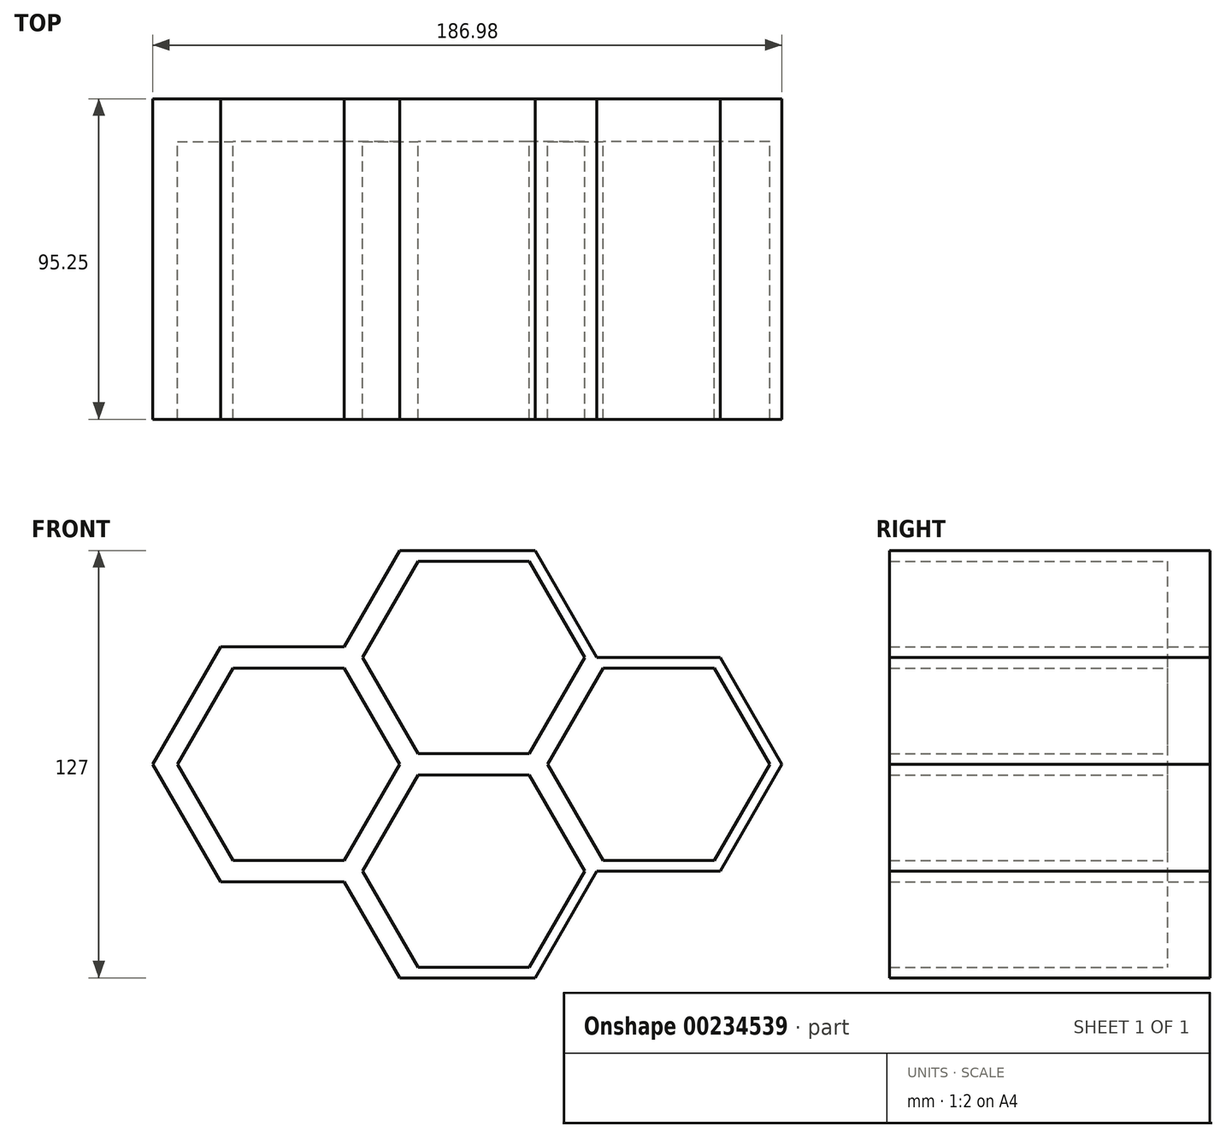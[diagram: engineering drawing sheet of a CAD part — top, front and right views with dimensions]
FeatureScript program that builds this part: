
annotation { "Feature Type Name" : "Feature", "Feature Type Description" : "" }
export const myFeature = defineFeature(function(context is Context, id is Id, definition is map)
    precondition{}
    {
        {
            var Q0;
            Q0=qCreatedBy(makeId("Front.planeOp"),FACE);
            var sketch = newSketch(context, id + "F0", { "sketchPlane" : qUnion([Q0])});
            skLineSegment(sketch, "E0.0", {"start": v(-77.6, 35.04) * mm, "end": v(-59.27, 66.8) * mm});
            skLineSegment(sketch, "E1.0", {"start": v(-132.6, 3.3) * mm, "end": v(-114.26, 35.04) * mm});
            skLineSegment(sketch, "E1.1", {"start": v(-114.26, 35.04) * mm, "end": v(-77.6, 35.04) * mm});
            skPoint(sketch, "E1.0.midPoint", {"position": v(-123.43, 19.17) * mm});
            skCircle(sketch, "E2.cCircle", {"center": v(-150.93, 35.04) * mm, "radius": 28.58 * mm, "construction": true});
            skLineSegment(sketch, "E2.0", {"start": v(-183.92, 35.04) * mm, "end": v(-167.42, 63.62) * mm});
            skLineSegment(sketch, "E2.1", {"start": v(-167.42, 63.62) * mm, "end": v(-134.43, 63.62) * mm});
            skLineSegment(sketch, "E2.2", {"start": v(-134.43, 63.62) * mm, "end": v(-117.93, 35.04) * mm});
            skLineSegment(sketch, "E2.3", {"start": v(-117.93, 35.04) * mm, "end": v(-134.43, 6.47) * mm});
            skLineSegment(sketch, "E2.4", {"start": v(-134.43, 6.47) * mm, "end": v(-167.42, 6.47) * mm});
            skLineSegment(sketch, "E2.5", {"start": v(-167.42, 6.47) * mm, "end": v(-183.92, 35.04) * mm});
            skPoint(sketch, "E2.0.midPoint", {"position": v(-175.67, 49.33) * mm});
            skCircle(sketch, "E3.cCircle", {"center": v(-150.93, 35.04) * mm, "radius": 31.75 * mm, "construction": true});
            skLineSegment(sketch, "E3.0", {"start": v(-187.59, 35.04) * mm, "end": v(-169.26, 66.8) * mm});
            skLineSegment(sketch, "E3.1", {"start": v(-169.26, 66.8) * mm, "end": v(-132.6, 66.8) * mm});
            skLineSegment(sketch, "E3.2", {"start": v(-132.6, 66.8) * mm, "end": v(-114.26, 35.04) * mm});
            skLineSegment(sketch, "E3.3", {"start": v(-114.26, 35.04) * mm, "end": v(-132.6, 3.3) * mm});
            skLineSegment(sketch, "E3.4", {"start": v(-132.6, 3.3) * mm, "end": v(-169.26, 3.3) * mm});
            skLineSegment(sketch, "E3.5", {"start": v(-169.26, 3.3) * mm, "end": v(-187.59, 35.04) * mm});
            skPoint(sketch, "E3.0.midPoint", {"position": v(-178.42, 50.92) * mm});
            skLineSegment(sketch, "E4.1", {"start": v(-221.8, 35.04) * mm, "end": v(-187.59, 35.04) * mm});
            skCircle(sketch, "E5.cCircle", {"center": v(-95.93, 66.8) * mm, "radius": 28.58 * mm, "construction": true});
            skLineSegment(sketch, "E5.0", {"start": v(-128.93, 66.8) * mm, "end": v(-112.43, 95.37) * mm});
            skLineSegment(sketch, "E5.1", {"start": v(-112.43, 95.37) * mm, "end": v(-79.43, 95.37) * mm});
            skLineSegment(sketch, "E5.2", {"start": v(-79.43, 95.37) * mm, "end": v(-62.94, 66.8) * mm});
            skLineSegment(sketch, "E5.3", {"start": v(-62.94, 66.8) * mm, "end": v(-79.43, 38.22) * mm});
            skLineSegment(sketch, "E5.4", {"start": v(-79.43, 38.22) * mm, "end": v(-112.43, 38.22) * mm});
            skLineSegment(sketch, "E5.5", {"start": v(-112.43, 38.22) * mm, "end": v(-128.93, 66.8) * mm});
            skPoint(sketch, "E5.0.midPoint", {"position": v(-120.68, 81.08) * mm});
            skCircle(sketch, "E6.cCircle", {"center": v(-95.93, 66.8) * mm, "radius": 31.75 * mm, "construction": true});
            skLineSegment(sketch, "E6.0", {"start": v(-132.6, 66.8) * mm, "end": v(-114.26, 98.54) * mm});
            skLineSegment(sketch, "E6.1", {"start": v(-114.26, 98.54) * mm, "end": v(-77.6, 98.54) * mm});
            skLineSegment(sketch, "E6.2", {"start": v(-77.6, 98.54) * mm, "end": v(-59.27, 66.8) * mm});
            skLineSegment(sketch, "E6.3", {"start": v(-59.27, 66.8) * mm, "end": v(-77.6, 35.04) * mm});
            skLineSegment(sketch, "E6.4", {"start": v(-77.6, 35.04) * mm, "end": v(-114.26, 35.04) * mm});
            skLineSegment(sketch, "E6.5", {"start": v(-114.26, 35.04) * mm, "end": v(-132.6, 66.8) * mm});
            skPoint(sketch, "E6.0.midPoint", {"position": v(-123.43, 82.67) * mm});
            skCircle(sketch, "E7.cCircle", {"center": v(-205.92, 66.8) * mm, "radius": 28.57 * mm, "construction": true});
            skLineSegment(sketch, "E7.0", {"start": v(-238.91, 66.8) * mm, "end": v(-222.42, 95.37) * mm});
            skLineSegment(sketch, "E7.1", {"start": v(-222.42, 95.37) * mm, "end": v(-189.42, 95.37) * mm});
            skLineSegment(sketch, "E7.2", {"start": v(-189.42, 95.37) * mm, "end": v(-172.92, 66.8) * mm});
            skLineSegment(sketch, "E7.3", {"start": v(-172.92, 66.8) * mm, "end": v(-189.42, 38.22) * mm});
            skLineSegment(sketch, "E7.4", {"start": v(-189.42, 38.22) * mm, "end": v(-222.42, 38.22) * mm});
            skLineSegment(sketch, "E7.5", {"start": v(-222.42, 38.22) * mm, "end": v(-238.91, 66.8) * mm});
            skPoint(sketch, "E7.0.midPoint", {"position": v(-230.66, 81.08) * mm});
            skCircle(sketch, "E8.cCircle", {"center": v(-205.92, 66.8) * mm, "radius": 31.75 * mm, "construction": true});
            skLineSegment(sketch, "E8.0", {"start": v(-242.58, 66.8) * mm, "end": v(-224.25, 98.54) * mm});
            skLineSegment(sketch, "E8.1", {"start": v(-224.25, 98.54) * mm, "end": v(-187.59, 98.54) * mm});
            skLineSegment(sketch, "E8.2", {"start": v(-187.59, 98.54) * mm, "end": v(-169.26, 66.8) * mm});
            skLineSegment(sketch, "E8.3", {"start": v(-169.26, 66.8) * mm, "end": v(-187.59, 35.04) * mm});
            skLineSegment(sketch, "E8.4", {"start": v(-187.59, 35.04) * mm, "end": v(-224.25, 35.04) * mm});
            skLineSegment(sketch, "E8.5", {"start": v(-224.25, 35.04) * mm, "end": v(-242.58, 66.8) * mm});
            skPoint(sketch, "E8.0.midPoint", {"position": v(-233.41, 82.67) * mm});
            skCircle(sketch, "E9.cCircle", {"center": v(-150.93, 98.54) * mm, "radius": 28.58 * mm, "construction": true});
            skLineSegment(sketch, "E9.0", {"start": v(-183.92, 98.54) * mm, "end": v(-167.42, 127.12) * mm});
            skLineSegment(sketch, "E9.1", {"start": v(-167.42, 127.12) * mm, "end": v(-134.43, 127.12) * mm});
            skLineSegment(sketch, "E9.2", {"start": v(-134.43, 127.12) * mm, "end": v(-117.93, 98.54) * mm});
            skLineSegment(sketch, "E9.3", {"start": v(-117.93, 98.54) * mm, "end": v(-134.43, 69.97) * mm});
            skLineSegment(sketch, "E9.4", {"start": v(-134.43, 69.97) * mm, "end": v(-167.42, 69.97) * mm});
            skLineSegment(sketch, "E9.5", {"start": v(-167.42, 69.97) * mm, "end": v(-183.92, 98.54) * mm});
            skPoint(sketch, "E9.0.midPoint", {"position": v(-175.67, 112.83) * mm});
            skCircle(sketch, "E10.cCircle", {"center": v(-150.93, 98.54) * mm, "radius": 31.75 * mm, "construction": true});
            skLineSegment(sketch, "E10.0", {"start": v(-187.59, 98.54) * mm, "end": v(-169.26, 130.3) * mm});
            skLineSegment(sketch, "E10.1", {"start": v(-169.26, 130.3) * mm, "end": v(-132.6, 130.3) * mm});
            skLineSegment(sketch, "E10.2", {"start": v(-132.6, 130.3) * mm, "end": v(-114.26, 98.54) * mm});
            skLineSegment(sketch, "E10.3", {"start": v(-114.26, 98.54) * mm, "end": v(-132.6, 66.8) * mm});
            skLineSegment(sketch, "E10.4", {"start": v(-132.6, 66.8) * mm, "end": v(-169.26, 66.8) * mm});
            skLineSegment(sketch, "E10.5", {"start": v(-169.26, 66.8) * mm, "end": v(-187.59, 98.54) * mm});
            skPoint(sketch, "E10.0.midPoint", {"position": v(-178.42, 114.42) * mm});
            skLineSegment(sketch, "E11.5", {"start": v(-59.27, 66.8) * mm, "end": v(-77.6, 98.54) * mm});
            skLineSegment(sketch, "E12.4", {"start": v(-77.6, 98.54) * mm, "end": v(-114.26, 98.54) * mm});
            skLineSegment(sketch, "E12.5", {"start": v(-114.26, 98.54) * mm, "end": v(-132.6, 130.3) * mm});
            skLineSegment(sketch, "E13.1", {"start": v(-169.26, 3.3) * mm, "end": v(-132.6, 3.3) * mm});
            skLineSegment(sketch, "E14.4", {"start": v(-190.64, 98.54) * mm, "end": v(-224.25, 98.54) * mm});
            skLineSegment(sketch, "E15.4", {"start": v(-132.6, 130.3) * mm, "end": v(-169.26, 130.3) * mm});
            skLineSegment(sketch, "E16", {"start": v(-172.92, 130.3) * mm, "end": v(-189.42, 101.72) * mm});
            skLineSegment(sketch, "E17", {"start": v(-189.42, 101.72) * mm, "end": v(-226.08, 101.72) * mm});
            skLineSegment(sketch, "E18", {"start": v(-226.08, 101.72) * mm, "end": v(-246.25, 66.8) * mm});
            skLineSegment(sketch, "E19", {"start": v(-246.25, 66.8) * mm, "end": v(-226.08, 31.87) * mm});
            skLineSegment(sketch, "E20", {"start": v(-226.08, 31.87) * mm, "end": v(-189.42, 31.87) * mm});
            skLineSegment(sketch, "E21", {"start": v(-189.42, 31.87) * mm, "end": v(-172.92, 3.3) * mm});
            skLineSegment(sketch, "E22", {"start": v(-73.94, 98.54) * mm, "end": v(-57.44, 69.97) * mm});
            skLineSegment(sketch, "E23", {"start": v(-172.92, 3.3) * mm, "end": v(-169.26, 3.3) * mm});
            skLineSegment(sketch, "E24", {"start": v(-169.26, 130.3) * mm, "end": v(-172.92, 130.3) * mm});
            skLineSegment(sketch, "E25", {"start": v(-57.44, 69.97) * mm, "end": v(-59.27, 66.8) * mm});
            skLineSegment(sketch, "E26", {"start": v(-73.94, 98.54) * mm, "end": v(-77.6, 98.54) * mm});
            skSolve(sketch);
        }
        {
            var Q0;
            Q0=makeQuery(id+"F0.imprint","IMPRINT",FACE,{"disambiguationData":[TD([[makeQuery(id+"F0.imprint","IMPRINT",EDGE,{"derivedFrom":sQuery(id+"F0.wireOp",EDGE,"68d16a58-0471-4e1c-b2b3-2a61df7c0d9d.0")}),-1.0]])]});
            var Q1;
            Q1=makeQuery(id+"F0.imprint","IMPRINT",FACE,{"disambiguationData":[TD([[makeQuery(id+"F0.imprint","IMPRINT",EDGE,{"derivedFrom":sQuery(id+"F0.wireOp",EDGE,"ae29455d-c252-400a-b569-c5a1c48e1351.0")}),-1.0]])]});
            var Q2;
            Q2=makeQuery(id+"F0.imprint","IMPRINT",FACE,{"disambiguationData":[TD([[makeQuery(id+"F0.imprint","IMPRINT",EDGE,{"derivedFrom":sQuery(id+"F0.wireOp",EDGE,"cad1e4f3-bd43-45ec-b31a-1d5006939c94.0")}),-1.0]])]});
            var Q3;
            Q3=makeQuery(id+"F0.imprint","IMPRINT",FACE,{"disambiguationData":[TD([[makeQuery(id+"F0.imprint","IMPRINT",EDGE,{"derivedFrom":sQuery(id+"F0.wireOp",EDGE,"b43d4d8c-f78a-4ff8-8565-99a66ce6ec5f.0")}),-1.0]])]});
            var Q4;
            Q4=makeQuery(id+"F0.imprint","IMPRINT",FACE,{"disambiguationData":[TD([[makeQuery(id+"F0.imprint","IMPRINT",EDGE,{"derivedFrom":sQuery(id+"F0.wireOp",EDGE,"8c75d941-d110-4871-aa41-90a72d60fb2b.0")}),-1.0]])]});
            var Q5;
            Q5=makeQuery(id+"F0.imprint","IMPRINT",FACE,{"disambiguationData":[TD([[makeQuery(id+"F0.imprint","IMPRINT",EDGE,{"derivedFrom":sQuery(id+"F0.wireOp",EDGE,"258573fa-3544-418e-8bc5-5d37e5b8ba09.0")}),-1.0]])]});
            var Q6;
            Q6=makeQuery(id+"F0.imprint","IMPRINT",FACE,{"disambiguationData":[TD([[makeQuery(id+"F0.imprint","IMPRINT",EDGE,{"derivedFrom":sQuery(id+"F0.wireOp",EDGE,"E7.0")}),-1.0]])]});
            var Q7;
            Q7=makeQuery(id+"F0.imprint","IMPRINT",FACE,{"disambiguationData":[TD([[makeQuery(id+"F0.imprint","IMPRINT",EDGE,{"derivedFrom":sQuery(id+"F0.wireOp",EDGE,"93717492-86db-456f-ae55-f71e4e93837b.0")}),-1.0]])]});
            var Q8;
            Q8=makeQuery(id+"F0.imprint","IMPRINT",FACE,{"disambiguationData":[TD([[makeQuery(id+"F0.imprint","IMPRINT",EDGE,{"derivedFrom":sQuery(id+"F0.wireOp",EDGE,"E9.0")}),-1.0]])]});
            var Q9;
            Q9=makeQuery(id+"F0.imprint","IMPRINT",FACE,{"disambiguationData":[TD([[makeQuery(id+"F0.imprint","IMPRINT",EDGE,{"derivedFrom":sQuery(id+"F0.wireOp",EDGE,"0306a0a6-7289-4661-a415-5fa5585f2cb5.0")}),-1.0]])]});
            var Q10;
            Q10=makeQuery(id+"F0.imprint","IMPRINT",FACE,{"disambiguationData":[TD([[makeQuery(id+"F0.imprint","IMPRINT",EDGE,{"derivedFrom":sQuery(id+"F0.wireOp",EDGE,"0a91a14e-ea0c-483f-91eb-c48bd73cb0e6.0")}),-1.0]])]});
            var Q11;
            Q11=makeQuery(id+"F0.imprint","IMPRINT",FACE,{"disambiguationData":[TD([[makeQuery(id+"F0.imprint","IMPRINT",EDGE,{"derivedFrom":sQuery(id+"F0.wireOp",EDGE,"cbfd9497-f7fe-4f18-9288-d90aa8075d81.0")}),-1.0]])]});
            var Q12;
            Q12=makeQuery(id+"F0.imprint","IMPRINT",FACE,{"disambiguationData":[TD([[makeQuery(id+"F0.imprint","IMPRINT",EDGE,{"derivedFrom":sQuery(id+"F0.wireOp",EDGE,"6282d196-dd8f-4bb0-bca4-b9108e277473.0")}),-1.0]])]});
            var Q13;
            Q13=makeQuery(id+"F0.imprint","IMPRINT",FACE,{"disambiguationData":[TD([[makeQuery(id+"F0.imprint","IMPRINT",EDGE,{"derivedFrom":sQuery(id+"F0.wireOp",EDGE,"084ca30c-4dc0-463f-bfd9-557787ed9a2f.0")}),-1.0]])]});
            var Q14;
            Q14=makeQuery(id+"F0.imprint","IMPRINT",FACE,{"disambiguationData":[TD([[makeQuery(id+"F0.imprint","IMPRINT",EDGE,{"derivedFrom":sQuery(id+"F0.wireOp",EDGE,"06c29831-6b25-410b-9247-4ee044b7735c.0")}),-1.0]])]});
            var Q15;
            Q15=makeQuery(id+"F0.imprint","IMPRINT",FACE,{"disambiguationData":[TD([[makeQuery(id+"F0.imprint","IMPRINT",EDGE,{"derivedFrom":sQuery(id+"F0.wireOp",EDGE,"b8eec94e-d97e-439b-aaac-63499233db4c.0")}),-1.0]])]});
            var Q16;
            Q16=makeQuery(id+"F0.imprint","IMPRINT",FACE,{"disambiguationData":[TD([[makeQuery(id+"F0.imprint","IMPRINT",EDGE,{"derivedFrom":sQuery(id+"F0.wireOp",EDGE,"2e929887-9bb9-4083-9cef-f9a6a24e8e46.0")}),-1.0]])]});
            var Q17;
            Q17=makeQuery(id+"F0.imprint","IMPRINT",FACE,{"disambiguationData":[TD([[makeQuery(id+"F0.imprint","IMPRINT",EDGE,{"derivedFrom":sQuery(id+"F0.wireOp",EDGE,"23671680-92ab-419e-a071-eb0943a5012b.0")}),-1.0]])]});
            var Q18;
            Q18=makeQuery(id+"F0.imprint","IMPRINT",FACE,{"disambiguationData":[TD([[makeQuery(id+"F0.imprint","IMPRINT",EDGE,{"derivedFrom":sQuery(id+"F0.wireOp",EDGE,"a1daa6ae-7864-4614-8fb9-3511dddc1266.0")}),-1.0]])]});
            var Q19;
            Q19=makeQuery(id+"F0.imprint","IMPRINT",FACE,{"disambiguationData":[TD([[makeQuery(id+"F0.imprint","IMPRINT",EDGE,{"derivedFrom":sQuery(id+"F0.wireOp",EDGE,"37efd634-c264-4683-8864-08b38c7986ca.0")}),-1.0]])]});
            var Q20;
            Q20=makeQuery(id+"F0.imprint","IMPRINT",FACE,{"disambiguationData":[TD([[makeQuery(id+"F0.imprint","IMPRINT",EDGE,{"derivedFrom":sQuery(id+"F0.wireOp",EDGE,"f2dd3995-374a-43c5-8725-4a87181dc8c5.0")}),-1.0]])]});
            var Q21;
            Q21=makeQuery(id+"F0.imprint","IMPRINT",FACE,{"disambiguationData":[TD([[makeQuery(id+"F0.imprint","IMPRINT",EDGE,{"derivedFrom":sQuery(id+"F0.wireOp",EDGE,"E2.0")}),-1.0]])]});
            var Q22;
            Q22=makeQuery(id+"F0.imprint","IMPRINT",FACE,{"disambiguationData":[TD([[makeQuery(id+"F0.imprint","IMPRINT",EDGE,{"derivedFrom":sQuery(id+"F0.wireOp",EDGE,"f97fdbdd-69fc-44f1-b8f7-f6a6a25558e6.0")}),-1.0]])]});
            var Q23;
            Q23=makeQuery(id+"F0.imprint","IMPRINT",FACE,{"disambiguationData":[TD([[makeQuery(id+"F0.imprint","IMPRINT",EDGE,{"derivedFrom":sQuery(id+"F0.wireOp",EDGE,"E5.0")}),-1.0]])]});
            var Q24;
            Q24=makeQuery(id+"F0.imprint","IMPRINT",FACE,{"disambiguationData":[TD([[makeQuery(id+"F0.imprint","IMPRINT",EDGE,{"derivedFrom":sQuery(id+"F0.wireOp",EDGE,"084ca30c-4dc0-463f-bfd9-557787ed9a2f.0")}),1.0]])]});
            var Q25;
            Q25=makeQuery(id+"F0.imprint","IMPRINT",FACE,{"disambiguationData":[TD([[makeQuery(id+"F0.imprint","IMPRINT",EDGE,{"derivedFrom":sQuery(id+"F0.wireOp",EDGE,"E2.0")}),1.0]])]});
            var Q26;
            Q26=makeQuery(id+"F0.imprint","IMPRINT",FACE,{"disambiguationData":[TD([[makeQuery(id+"F0.imprint","IMPRINT",EDGE,{"derivedFrom":sQuery(id+"F0.wireOp",EDGE,"23671680-92ab-419e-a071-eb0943a5012b.0")}),1.0]])]});
            var Q27;
            Q27=makeQuery(id+"F0.imprint","IMPRINT",FACE,{"disambiguationData":[TD([[makeQuery(id+"F0.imprint","IMPRINT",EDGE,{"derivedFrom":sQuery(id+"F0.wireOp",EDGE,"2e929887-9bb9-4083-9cef-f9a6a24e8e46.0")}),1.0]])]});
            var Q28;
            Q28=makeQuery(id+"F0.imprint","IMPRINT",FACE,{"disambiguationData":[TD([[makeQuery(id+"F0.imprint","IMPRINT",EDGE,{"derivedFrom":sQuery(id+"F0.wireOp",EDGE,"E5.0")}),1.0]])]});
            var Q29;
            Q29=makeQuery(id+"F0.imprint","IMPRINT",FACE,{"disambiguationData":[TD([[makeQuery(id+"F0.imprint","IMPRINT",EDGE,{"derivedFrom":sQuery(id+"F0.wireOp",EDGE,"b43d4d8c-f78a-4ff8-8565-99a66ce6ec5f.0")}),1.0]])]});
            var Q30;
            Q30=makeQuery(id+"F0.imprint","IMPRINT",FACE,{"disambiguationData":[TD([[makeQuery(id+"F0.imprint","IMPRINT",EDGE,{"derivedFrom":sQuery(id+"F0.wireOp",EDGE,"ae29455d-c252-400a-b569-c5a1c48e1351.0")}),1.0]])]});
            var Q31;
            Q31=makeQuery(id+"F0.imprint","IMPRINT",FACE,{"disambiguationData":[TD([[makeQuery(id+"F0.imprint","IMPRINT",EDGE,{"derivedFrom":sQuery(id+"F0.wireOp",EDGE,"0a91a14e-ea0c-483f-91eb-c48bd73cb0e6.0")}),1.0]])]});
            var Q32;
            Q32=makeQuery(id+"F0.imprint","IMPRINT",FACE,{"disambiguationData":[TD([[makeQuery(id+"F0.imprint","IMPRINT",EDGE,{"derivedFrom":sQuery(id+"F0.wireOp",EDGE,"258573fa-3544-418e-8bc5-5d37e5b8ba09.0")}),1.0]])]});
            var Q33;
            Q33=makeQuery(id+"F0.imprint","IMPRINT",FACE,{"disambiguationData":[TD([[makeQuery(id+"F0.imprint","IMPRINT",EDGE,{"derivedFrom":sQuery(id+"F0.wireOp",EDGE,"cbfd9497-f7fe-4f18-9288-d90aa8075d81.0")}),1.0]])]});
            var Q34;
            Q34=makeQuery(id+"F0.imprint","IMPRINT",FACE,{"disambiguationData":[TD([[makeQuery(id+"F0.imprint","IMPRINT",EDGE,{"derivedFrom":sQuery(id+"F0.wireOp",EDGE,"f97fdbdd-69fc-44f1-b8f7-f6a6a25558e6.0")}),1.0]])]});
            var Q35;
            Q35=makeQuery(id+"F0.imprint","IMPRINT",FACE,{"disambiguationData":[TD([[makeQuery(id+"F0.imprint","IMPRINT",EDGE,{"derivedFrom":sQuery(id+"F0.wireOp",EDGE,"b8eec94e-d97e-439b-aaac-63499233db4c.0")}),1.0]])]});
            var Q36;
            Q36=makeQuery(id+"F0.imprint","IMPRINT",FACE,{"disambiguationData":[TD([[makeQuery(id+"F0.imprint","IMPRINT",EDGE,{"derivedFrom":sQuery(id+"F0.wireOp",EDGE,"8c75d941-d110-4871-aa41-90a72d60fb2b.0")}),1.0]])]});
            var Q37;
            Q37=makeQuery(id+"F0.imprint","IMPRINT",FACE,{"disambiguationData":[TD([[makeQuery(id+"F0.imprint","IMPRINT",EDGE,{"derivedFrom":sQuery(id+"F0.wireOp",EDGE,"E9.0")}),1.0]])]});
            var Q38;
            Q38=makeQuery(id+"F0.imprint","IMPRINT",FACE,{"disambiguationData":[TD([[makeQuery(id+"F0.imprint","IMPRINT",EDGE,{"derivedFrom":sQuery(id+"F0.wireOp",EDGE,"37efd634-c264-4683-8864-08b38c7986ca.0")}),1.0]])]});
            var Q39;
            Q39=makeQuery(id+"F0.imprint","IMPRINT",FACE,{"disambiguationData":[TD([[makeQuery(id+"F0.imprint","IMPRINT",EDGE,{"derivedFrom":sQuery(id+"F0.wireOp",EDGE,"68d16a58-0471-4e1c-b2b3-2a61df7c0d9d.0")}),1.0]])]});
            var Q40;
            Q40=makeQuery(id+"F0.imprint","IMPRINT",FACE,{"disambiguationData":[TD([[makeQuery(id+"F0.imprint","IMPRINT",EDGE,{"derivedFrom":sQuery(id+"F0.wireOp",EDGE,"0306a0a6-7289-4661-a415-5fa5585f2cb5.0")}),1.0]])]});
            var Q41;
            Q41=makeQuery(id+"F0.imprint","IMPRINT",FACE,{"disambiguationData":[TD([[makeQuery(id+"F0.imprint","IMPRINT",EDGE,{"derivedFrom":sQuery(id+"F0.wireOp",EDGE,"E7.0")}),1.0]])]});
            var Q42;
            Q42=makeQuery(id+"F0.imprint","IMPRINT",FACE,{"disambiguationData":[TD([[makeQuery(id+"F0.imprint","IMPRINT",EDGE,{"derivedFrom":sQuery(id+"F0.wireOp",EDGE,"06c29831-6b25-410b-9247-4ee044b7735c.0")}),1.0]])]});
            var Q43;
            Q43=makeQuery(id+"F0.imprint","IMPRINT",FACE,{"disambiguationData":[TD([[makeQuery(id+"F0.imprint","IMPRINT",EDGE,{"derivedFrom":sQuery(id+"F0.wireOp",EDGE,"6282d196-dd8f-4bb0-bca4-b9108e277473.0")}),1.0]])]});
            var Q44;
            Q44=makeQuery(id+"F0.imprint","IMPRINT",FACE,{"disambiguationData":[TD([[makeQuery(id+"F0.imprint","IMPRINT",EDGE,{"derivedFrom":sQuery(id+"F0.wireOp",EDGE,"cad1e4f3-bd43-45ec-b31a-1d5006939c94.0")}),1.0]])]});
            var Q45;
            Q45=makeQuery(id+"F0.imprint","IMPRINT",FACE,{"disambiguationData":[TD([[makeQuery(id+"F0.imprint","IMPRINT",EDGE,{"derivedFrom":sQuery(id+"F0.wireOp",EDGE,"f2dd3995-374a-43c5-8725-4a87181dc8c5.0")}),1.0]])]});
            var Q46;
            Q46=makeQuery(id+"F0.imprint","IMPRINT",FACE,{"disambiguationData":[TD([[makeQuery(id+"F0.imprint","IMPRINT",EDGE,{"derivedFrom":sQuery(id+"F0.wireOp",EDGE,"a1daa6ae-7864-4614-8fb9-3511dddc1266.0")}),1.0]])]});
            var Q47;
            Q47=makeQuery(id+"F0.imprint","IMPRINT",FACE,{"disambiguationData":[TD([[makeQuery(id+"F0.imprint","IMPRINT",EDGE,{"derivedFrom":sQuery(id+"F0.wireOp",EDGE,"93717492-86db-456f-ae55-f71e4e93837b.0")}),1.0]])]});
            extrude(context, id + "F1", {"entities" : qUnion([Q0, Q1, Q2, Q3, Q4, Q5, Q6, Q7, Q8, Q9, Q10, Q11, Q12, Q13, Q14, Q15, Q16, Q17, Q18, Q19, Q20, Q21, Q22, Q23, Q24, Q25, Q26, Q27, Q28, Q29, Q30, Q31, Q32, Q33, Q34, Q35, Q36, Q37, Q38, Q39, Q40, Q41, Q42, Q43, Q44, Q45, Q46, Q47]), "depth" : 12.7 * mm});
        }
        {
            var Q0;
            Q0=makeQuery(id+"F0.imprint","IMPRINT",FACE,{"disambiguationData":[TD([[makeQuery(id+"F0.imprint","IMPRINT",EDGE,{"derivedFrom":sQuery(id+"F0.wireOp",EDGE,"8c75d941-d110-4871-aa41-90a72d60fb2b.0")}),1.0]])]});
            var Q1;
            Q1=makeQuery(id+"F0.imprint","IMPRINT",FACE,{"disambiguationData":[TD([[makeQuery(id+"F0.imprint","IMPRINT",EDGE,{"derivedFrom":sQuery(id+"F0.wireOp",EDGE,"b8eec94e-d97e-439b-aaac-63499233db4c.0")}),1.0]])]});
            var Q2;
            Q2=makeQuery(id+"F0.imprint","IMPRINT",FACE,{"disambiguationData":[TD([[makeQuery(id+"F0.imprint","IMPRINT",EDGE,{"derivedFrom":sQuery(id+"F0.wireOp",EDGE,"cad1e4f3-bd43-45ec-b31a-1d5006939c94.0")}),1.0]])]});
            var Q3;
            Q3=makeQuery(id+"F0.imprint","IMPRINT",FACE,{"disambiguationData":[TD([[makeQuery(id+"F0.imprint","IMPRINT",EDGE,{"derivedFrom":sQuery(id+"F0.wireOp",EDGE,"68d16a58-0471-4e1c-b2b3-2a61df7c0d9d.0")}),1.0]])]});
            var Q4;
            Q4=makeQuery(id+"F0.imprint","IMPRINT",FACE,{"disambiguationData":[TD([[makeQuery(id+"F0.imprint","IMPRINT",EDGE,{"derivedFrom":sQuery(id+"F0.wireOp",EDGE,"0306a0a6-7289-4661-a415-5fa5585f2cb5.0")}),1.0]])]});
            var Q5;
            Q5=makeQuery(id+"F0.imprint","IMPRINT",FACE,{"disambiguationData":[TD([[makeQuery(id+"F0.imprint","IMPRINT",EDGE,{"derivedFrom":sQuery(id+"F0.wireOp",EDGE,"084ca30c-4dc0-463f-bfd9-557787ed9a2f.0")}),1.0]])]});
            var Q6;
            Q6=makeQuery(id+"F0.imprint","IMPRINT",FACE,{"disambiguationData":[TD([[makeQuery(id+"F0.imprint","IMPRINT",EDGE,{"derivedFrom":sQuery(id+"F0.wireOp",EDGE,"E5.0")}),1.0]])]});
            var Q7;
            Q7=makeQuery(id+"F0.imprint","IMPRINT",FACE,{"disambiguationData":[TD([[makeQuery(id+"F0.imprint","IMPRINT",EDGE,{"derivedFrom":sQuery(id+"F0.wireOp",EDGE,"a1daa6ae-7864-4614-8fb9-3511dddc1266.0")}),1.0]])]});
            var Q8;
            Q8=makeQuery(id+"F0.imprint","IMPRINT",FACE,{"disambiguationData":[TD([[makeQuery(id+"F0.imprint","IMPRINT",EDGE,{"derivedFrom":sQuery(id+"F0.wireOp",EDGE,"93717492-86db-456f-ae55-f71e4e93837b.0")}),1.0]])]});
            var Q9;
            Q9=makeQuery(id+"F0.imprint","IMPRINT",FACE,{"disambiguationData":[TD([[makeQuery(id+"F0.imprint","IMPRINT",EDGE,{"derivedFrom":sQuery(id+"F0.wireOp",EDGE,"258573fa-3544-418e-8bc5-5d37e5b8ba09.0")}),1.0]])]});
            var Q10;
            Q10=makeQuery(id+"F0.imprint","IMPRINT",FACE,{"disambiguationData":[TD([[makeQuery(id+"F0.imprint","IMPRINT",EDGE,{"derivedFrom":sQuery(id+"F0.wireOp",EDGE,"f2dd3995-374a-43c5-8725-4a87181dc8c5.0")}),1.0]])]});
            var Q11;
            Q11=makeQuery(id+"F0.imprint","IMPRINT",FACE,{"disambiguationData":[TD([[makeQuery(id+"F0.imprint","IMPRINT",EDGE,{"derivedFrom":sQuery(id+"F0.wireOp",EDGE,"23671680-92ab-419e-a071-eb0943a5012b.0")}),1.0]])]});
            var Q12;
            Q12=makeQuery(id+"F0.imprint","IMPRINT",FACE,{"disambiguationData":[TD([[makeQuery(id+"F0.imprint","IMPRINT",EDGE,{"derivedFrom":sQuery(id+"F0.wireOp",EDGE,"06c29831-6b25-410b-9247-4ee044b7735c.0")}),1.0]])]});
            var Q13;
            Q13=makeQuery(id+"F0.imprint","IMPRINT",FACE,{"disambiguationData":[TD([[makeQuery(id+"F0.imprint","IMPRINT",EDGE,{"derivedFrom":sQuery(id+"F0.wireOp",EDGE,"ae29455d-c252-400a-b569-c5a1c48e1351.0")}),1.0]])]});
            var Q14;
            Q14=makeQuery(id+"F0.imprint","IMPRINT",FACE,{"disambiguationData":[TD([[makeQuery(id+"F0.imprint","IMPRINT",EDGE,{"derivedFrom":sQuery(id+"F0.wireOp",EDGE,"f97fdbdd-69fc-44f1-b8f7-f6a6a25558e6.0")}),1.0]])]});
            var Q15;
            Q15=makeQuery(id+"F0.imprint","IMPRINT",FACE,{"disambiguationData":[TD([[makeQuery(id+"F0.imprint","IMPRINT",EDGE,{"derivedFrom":sQuery(id+"F0.wireOp",EDGE,"2e929887-9bb9-4083-9cef-f9a6a24e8e46.0")}),1.0]])]});
            var Q16;
            Q16=makeQuery(id+"F0.imprint","IMPRINT",FACE,{"disambiguationData":[TD([[makeQuery(id+"F0.imprint","IMPRINT",EDGE,{"derivedFrom":sQuery(id+"F0.wireOp",EDGE,"0a91a14e-ea0c-483f-91eb-c48bd73cb0e6.0")}),1.0]])]});
            var Q17;
            Q17=makeQuery(id+"F0.imprint","IMPRINT",FACE,{"disambiguationData":[TD([[makeQuery(id+"F0.imprint","IMPRINT",EDGE,{"derivedFrom":sQuery(id+"F0.wireOp",EDGE,"37efd634-c264-4683-8864-08b38c7986ca.0")}),1.0]])]});
            var Q18;
            Q18=makeQuery(id+"F0.imprint","IMPRINT",FACE,{"disambiguationData":[TD([[makeQuery(id+"F0.imprint","IMPRINT",EDGE,{"derivedFrom":sQuery(id+"F0.wireOp",EDGE,"cbfd9497-f7fe-4f18-9288-d90aa8075d81.0")}),1.0]])]});
            var Q19;
            Q19=makeQuery(id+"F0.imprint","IMPRINT",FACE,{"disambiguationData":[TD([[makeQuery(id+"F0.imprint","IMPRINT",EDGE,{"derivedFrom":sQuery(id+"F0.wireOp",EDGE,"6282d196-dd8f-4bb0-bca4-b9108e277473.0")}),1.0]])]});
            var Q20;
            Q20=makeQuery(id+"F0.imprint","IMPRINT",FACE,{"disambiguationData":[TD([[makeQuery(id+"F0.imprint","IMPRINT",EDGE,{"derivedFrom":sQuery(id+"F0.wireOp",EDGE,"E7.0")}),1.0]])]});
            var Q21;
            Q21=makeQuery(id+"F0.imprint","IMPRINT",FACE,{"disambiguationData":[TD([[makeQuery(id+"F0.imprint","IMPRINT",EDGE,{"derivedFrom":sQuery(id+"F0.wireOp",EDGE,"b43d4d8c-f78a-4ff8-8565-99a66ce6ec5f.0")}),1.0]])]});
            var Q22;
            Q22=makeQuery(id+"F0.imprint","IMPRINT",FACE,{"disambiguationData":[TD([[makeQuery(id+"F0.imprint","IMPRINT",EDGE,{"derivedFrom":sQuery(id+"F0.wireOp",EDGE,"E9.0")}),1.0]])]});
            var Q23;
            Q23=makeQuery(id+"F0.imprint","IMPRINT",FACE,{"disambiguationData":[TD([[makeQuery(id+"F0.imprint","IMPRINT",EDGE,{"derivedFrom":sQuery(id+"F0.wireOp",EDGE,"E2.0")}),1.0]])]});
            var Q24;
            {var subQ6=sQuery(id+"F0.wireOp",EDGE,"E0.3");Q24=makeQuery(id+"F0.imprint","IMPRINT",FACE,{"disambiguationData":[TD([[makeQuery(id+"F0.imprint","IMPRINT",EDGE,{"derivedFrom":subQ6}),1.0]])]});}
            var Q25;
            Q25=makeQuery(id+"F0.imprint","IMPRINT",FACE,{"disambiguationData":[TD([[makeQuery(id+"F0.imprint","IMPRINT",EDGE,{"derivedFrom":sQuery(id+"F0.wireOp",EDGE,"E0.1")}),1.0]])]});
            var Q26;
            {var subQ3=sQuery(id+"F0.wireOp",EDGE,"E3.5");Q26=makeQuery(id+"F0.imprint","IMPRINT",FACE,{"disambiguationData":[TD([[makeQuery(id+"F0.imprint","IMPRINT",EDGE,{"derivedFrom":subQ3}),1.0]])]});}
            var Q27;
            Q27=makeQuery(id+"F0.imprint","IMPRINT",FACE,{"disambiguationData":[TD([[makeQuery(id+"F0.imprint","IMPRINT",EDGE,{"derivedFrom":sQuery(id+"F0.wireOp",EDGE,"E11.5")}),-1.0]])]});
            extrude(context, id + "F2", {"entities" : qUnion([Q0, Q1, Q2, Q3, Q4, Q5, Q6, Q7, Q8, Q9, Q10, Q11, Q12, Q13, Q14, Q15, Q16, Q17, Q18, Q19, Q20, Q21, Q22, Q23, Q24, Q25, Q26, Q27]), "operationType" : NewBodyOperationType.ADD, "depth" : 95.25 * mm});
        }
    });
